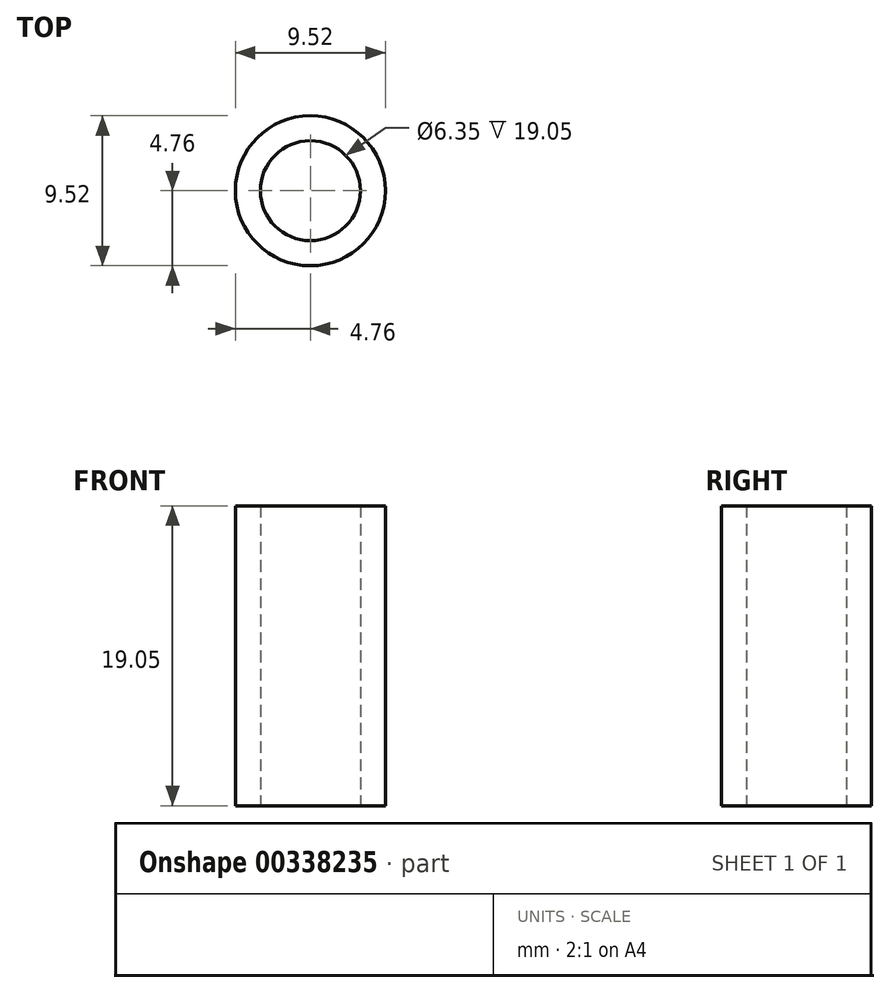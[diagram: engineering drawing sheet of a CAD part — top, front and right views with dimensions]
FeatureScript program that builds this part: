
annotation { "Feature Type Name" : "Feature", "Feature Type Description" : "" }
export const myFeature = defineFeature(function(context is Context, id is Id, definition is map)
    precondition{}
    {
        {
            var Q0;
            Q0=qCreatedBy(makeId("Top.planeOp"),FACE);
            var sketch = newSketch(context, id + "F0", { "sketchPlane" : qUnion([Q0])});
            skCircle(sketch, "E0", {"center": v(0, 0) * mm, "radius": 3.18 * mm});
            skCircle(sketch, "E1", {"center": v(0, 0) * mm, "radius": 4.76 * mm});
            skSolve(sketch);
        }
        {
            var Q0;
            Q0 = qSketchRegion(id + "F0", true);
            extrude(context, id + "F1", {"entities" : qUnion([Q0]), "depth" : 19.05 * mm});
        }
    });
